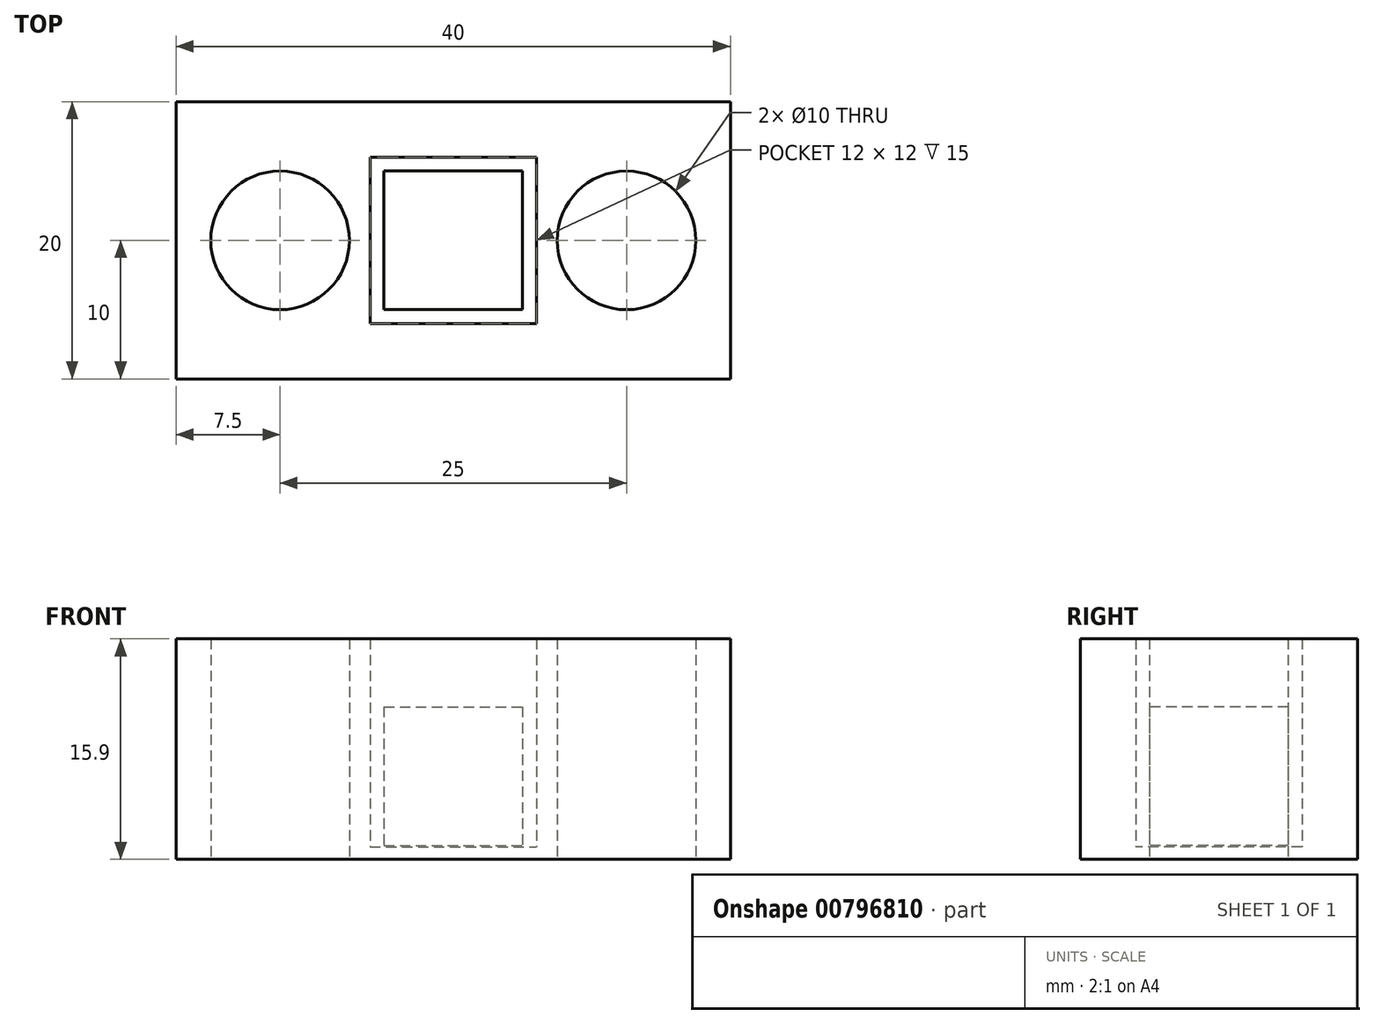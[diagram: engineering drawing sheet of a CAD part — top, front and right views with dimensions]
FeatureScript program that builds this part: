
annotation { "Feature Type Name" : "Feature", "Feature Type Description" : "" }
export const myFeature = defineFeature(function(context is Context, id is Id, definition is map)
    precondition{}
    {
        {
            var Q0;
            Q0=qCreatedBy(makeId("Top.planeOp"),FACE);
            var sketch = newSketch(context, id + "F0", { "sketchPlane" : qUnion([Q0])});
            skLineSegment(sketch, "E0.bottom", {"start": v(-5, 5) * mm, "end": v(5, 5) * mm});
            skLineSegment(sketch, "E0.top", {"start": v(-5, -5) * mm, "end": v(5, -5) * mm});
            skLineSegment(sketch, "E0.left", {"start": v(-5, 5) * mm, "end": v(-5, -5) * mm});
            skLineSegment(sketch, "E0.right", {"start": v(5, 5) * mm, "end": v(5, -5) * mm});
            skLineSegment(sketch, "E1", {"start": v(0, 5) * mm, "end": v(0, -5) * mm, "construction": true});
            skLineSegment(sketch, "E2", {"start": v(-5, 0) * mm, "end": v(5, 0) * mm, "construction": true});
            skSolve(sketch);
        }
        {
            var Q0;
            Q0 = qSketchRegion(id + "F0", true);
            extrude(context, id + "F1", {"entities" : qUnion([Q0]), "depth" : 10 * mm, "offsetDistance" : 25 * mm});
        }
        {
            var Q0;
            Q0=makeQuery(id+"F1.opExtrude","CAP_FACE",FACE,{"disambiguationData":[OSD([sQuery(id+"F0.wireOp",EDGE,"E0.bottom"),sQuery(id+"F0.wireOp",EDGE,"E0.top"),sQuery(id+"F0.wireOp",EDGE,"E0.left"),sQuery(id+"F0.wireOp",EDGE,"E0.right")])],"isStart":true});
            cPlane(context, id + "F2", {"entities" : qUnion([Q0]), "cplaneType" : CPlaneType.OFFSET, "offset" : 1 * mm, "width" : 150 * mm, "height" : 150 * mm});
        }
        {
            var Q0;
            Q0=qCreatedBy(id+"F2.planeOp",FACE);
            var sketch = newSketch(context, id + "F3", { "sketchPlane" : qUnion([Q0])});
            skLineSegment(sketch, "E3.bottom", {"start": v(-20, 10) * mm, "end": v(20, 10) * mm});
            skLineSegment(sketch, "E3.top", {"start": v(-20, -10) * mm, "end": v(20, -10) * mm});
            skLineSegment(sketch, "E3.left", {"start": v(-20, 10) * mm, "end": v(-20, -10) * mm});
            skLineSegment(sketch, "E3.right", {"start": v(20, 10) * mm, "end": v(20, -10) * mm});
            skLineSegment(sketch, "E4", {"start": v(0, 10) * mm, "end": v(0, -10) * mm, "construction": true});
            skLineSegment(sketch, "E5", {"start": v(20, 0) * mm, "end": v(-20, 0) * mm, "construction": true});
            skLineSegment(sketch, "E6.0", {"start": v(-5, 5) * mm, "end": v(5, 5) * mm, "construction": true});
            skLineSegment(sketch, "E7", {"start": v(0, 5) * mm, "end": v(0, 10) * mm, "construction": true});
            skLineSegment(sketch, "E8.0", {"start": v(5, -5) * mm, "end": v(5, 5) * mm, "construction": true});
            skLineSegment(sketch, "E9", {"start": v(5, 0) * mm, "end": v(20, 0) * mm, "construction": true});
            skLineSegment(sketch, "E10", {"start": v(5, 0) * mm, "end": v(12.5, 0) * mm, "construction": true});
            skCircle(sketch, "E11", {"center": v(12.5, 0) * mm, "radius": 5 * mm});
            skCircle(sketch, "E12.MirrorC", {"center": v(-12.5, 0) * mm, "radius": 5 * mm});
            skSolve(sketch);
        }
        {
            var Q0;
            Q0=makeQuery(id+"F3.imprint","IMPRINT",FACE,{"disambiguationData":[TD([[makeQuery(id+"F3.imprint","IMPRINT",EDGE,{"derivedFrom":sQuery(id+"F3.wireOp",EDGE,"E3.bottom")}),-1.0]])]});
            var Q1;
            Q1=makeQuery(id+"F1.opExtrude","CAP_FACE",FACE,{"disambiguationData":[OSD([sQuery(id+"F0.wireOp",EDGE,"E0.bottom"),sQuery(id+"F0.wireOp",EDGE,"E0.top"),sQuery(id+"F0.wireOp",EDGE,"E0.left"),sQuery(id+"F0.wireOp",EDGE,"E0.right")])],"isStart":true});
            extrude(context, id + "F4", {"entities" : qUnion([Q0]), "operationType" : NewBodyOperationType.ADD, "oppositeDirection" : true, "depth" : 0.9 * mm, "endBoundEntityFace" : qUnion([Q1]), "offsetDistance" : 25 * mm});
        }
        {
            var Q0;
            Q0=makeQuery(id+"F4.opExtrude","CAP_FACE",FACE,{"disambiguationData":[OSD([sQuery(id+"F3.wireOp",EDGE,"E3.bottom"),sQuery(id+"F3.wireOp",EDGE,"E3.top"),sQuery(id+"F3.wireOp",EDGE,"E3.left"),sQuery(id+"F3.wireOp",EDGE,"E3.right"),sQuery(id+"F3.wireOp",EDGE,"E11"),sQuery(id+"F3.wireOp",EDGE,"E12.MirrorC")])],"isStart":false});
            var sketch = newSketch(context, id + "F5", { "sketchPlane" : qUnion([Q0])});
            skLineSegment(sketch, "E13.0", {"start": v(-5, 5) * mm, "end": v(5, 5) * mm, "construction": true});
            skLineSegment(sketch, "E14.0", {"start": v(5, 5) * mm, "end": v(5, -5) * mm, "construction": true});
            skLineSegment(sketch, "E15.0", {"start": v(0, 5) * mm, "end": v(0, -5) * mm, "construction": true});
            skLineSegment(sketch, "E16.0", {"start": v(-5, 0) * mm, "end": v(5, 0) * mm, "construction": true});
            skLineSegment(sketch, "E17", {"start": v(5, 5) * mm, "end": v(5, 6) * mm, "construction": true});
            skLineSegment(sketch, "E18", {"start": v(5, 5) * mm, "end": v(6, 5) * mm, "construction": true});
            skLineSegment(sketch, "E19", {"start": v(6, 6) * mm, "end": v(0, 6) * mm});
            skLineSegment(sketch, "E20.MirrorCS", {"start": v(-6, 6) * mm, "end": v(0, 6) * mm});
            skLineSegment(sketch, "E21.MirrorCS", {"start": v(6, -6) * mm, "end": v(0, -6) * mm});
            skLineSegment(sketch, "E22.MirrorCS", {"start": v(-6, -6) * mm, "end": v(0, -6) * mm});
            skLineSegment(sketch, "E23", {"start": v(-6, 6) * mm, "end": v(-6, -6) * mm});
            skLineSegment(sketch, "E24", {"start": v(6, 6) * mm, "end": v(6, -6) * mm});
            skSolve(sketch);
        }
        {
            var Q0;
            Q0=makeQuery(id+"F5.imprint","IMPRINT",FACE,{"disambiguationData":[TD([[makeQuery(id+"F5.imprint","IMPRINT",EDGE,{"derivedFrom":sQuery(id+"F5.wireOp",EDGE,"E19")}),-1.0]])]});
            extrude(context, id + "F6", {"entities" : qUnion([Q0]), "operationType" : NewBodyOperationType.ADD, "depth" : 15 * mm, "offsetDistance" : 25 * mm});
        }
    });
